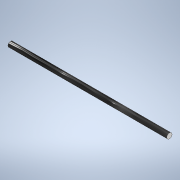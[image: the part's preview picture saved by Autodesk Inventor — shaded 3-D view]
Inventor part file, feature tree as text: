
AUTODESK INVENTOR PART (.ipt)
format: ipt  version: 2021 (Build 250183000, 183)  size: 102,400 bytes
history: native  units: in
note: dims shown in document units (in); Inventor stores cm internally (conversion verified against a paired STEP export)
features: extrude x1, sketch x1
ambient origin geometry x8: Origin, YZ Plane, XZ Plane, XY Plane, X Axis, Y Axis, Z Axis, Center Point
bodies: Solid1 (feature_tree)
feature tree (2):
  extrude  "Extrusion1"  Depth=0.1614in TaperAngle=0.0deg
  sketch  "Sketch1"  dims[d0=0.0053in d1=0.1614in d2=0.0in]
